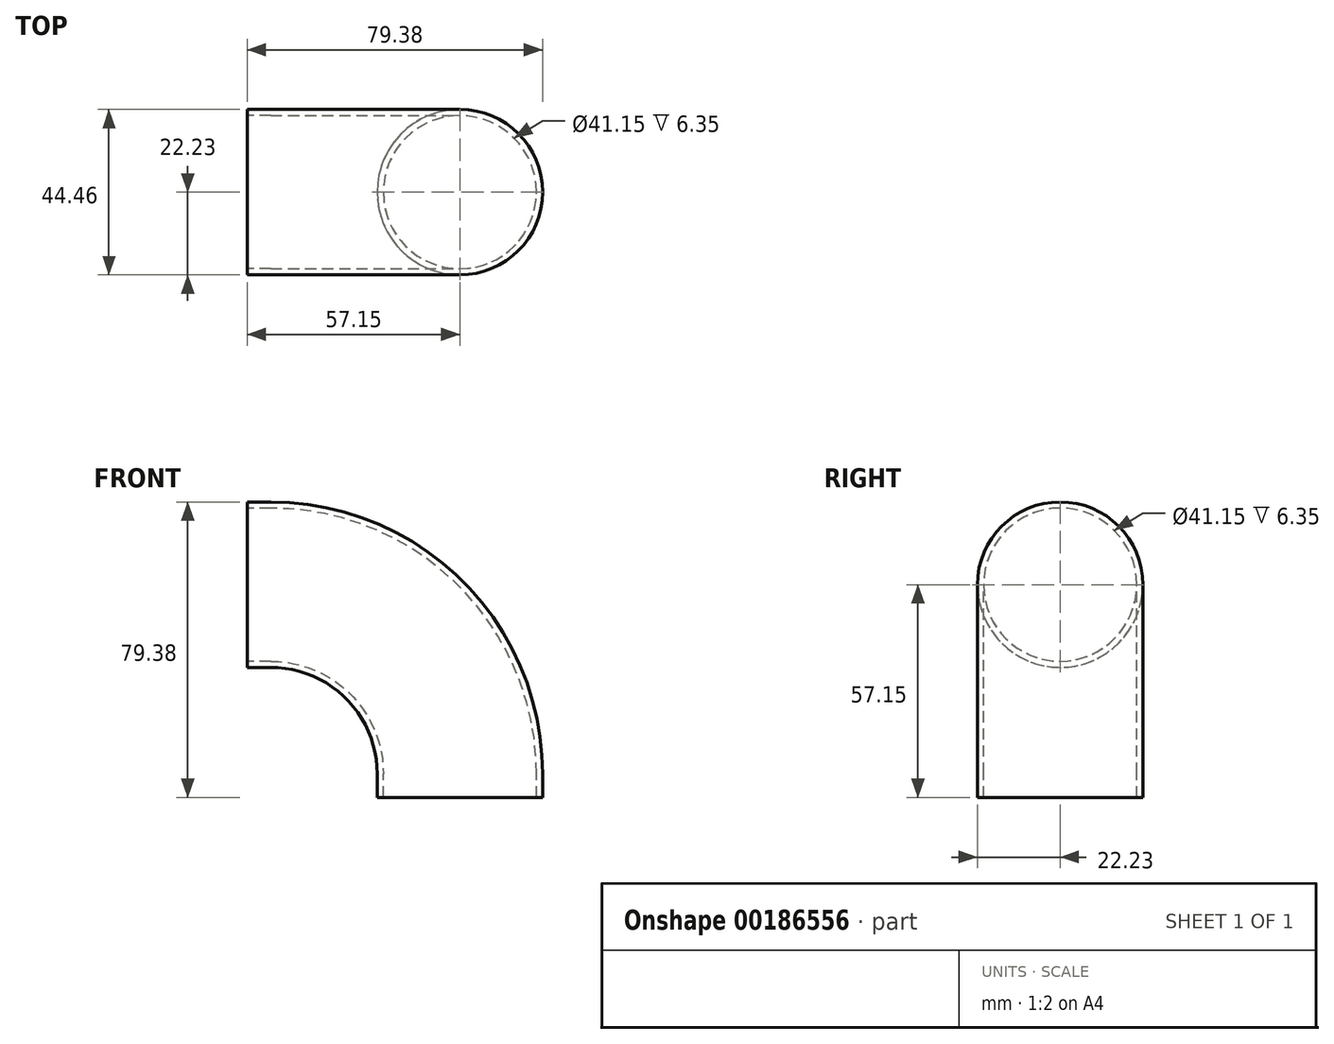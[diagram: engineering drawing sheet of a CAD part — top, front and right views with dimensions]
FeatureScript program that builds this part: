
annotation { "Feature Type Name" : "Feature", "Feature Type Description" : "" }
export const myFeature = defineFeature(function(context is Context, id is Id, definition is map)
    precondition{}
    {
        {
            var Q0;
            Q0=qCreatedBy(makeId("Front.planeOp"),FACE);
            var sketch = newSketch(context, id + "F0", { "sketchPlane" : qUnion([Q0])});
            skPoint(sketch, "E0.visualSharp", {"position": v(0, 41.92) * mm});
            skLineSegment(sketch, "E1", {"start": v(0, 0) * mm, "end": v(0, 6.35) * mm});
            skLineSegment(sketch, "E2", {"start": v(-50.8, 57.15) * mm, "end": v(-57.15, 57.15) * mm});
            skPoint(sketch, "E3.visualSharp", {"position": v(0, 57.15) * mm});
            skArc(sketch, "E3.filletArc", {"start": v(0, 6.35) * mm, "mid": v(-14.88, 42.27) * mm, "end": v(-50.8, 57.15) * mm});
            skSolve(sketch);
        }
        {
            var Q0;
            Q0=qCreatedBy(makeId("Top.planeOp"),FACE);
            var sketch = newSketch(context, id + "F1", { "sketchPlane" : qUnion([Q0])});
            skCircle(sketch, "E4", {"center": v(0, 0) * mm, "radius": 22.23 * mm});
            skCircle(sketch, "E5", {"center": v(0, 0) * mm, "radius": 20.57 * mm});
            skSolve(sketch);
        }
        {
            var Q0;
            Q0 = qSketchRegion(id + "F1", true);
            var Q1;
            Q1 = qConstructionFilter(qBodyType(qCreatedBy(id + "F0" ,EDGE), BodyType.WIRE), ConstructionObject.NO);
            sweep(context, id + "F2", {"profiles" : qUnion([Q0]), "path" : qUnion([Q1])});
        }
    });
